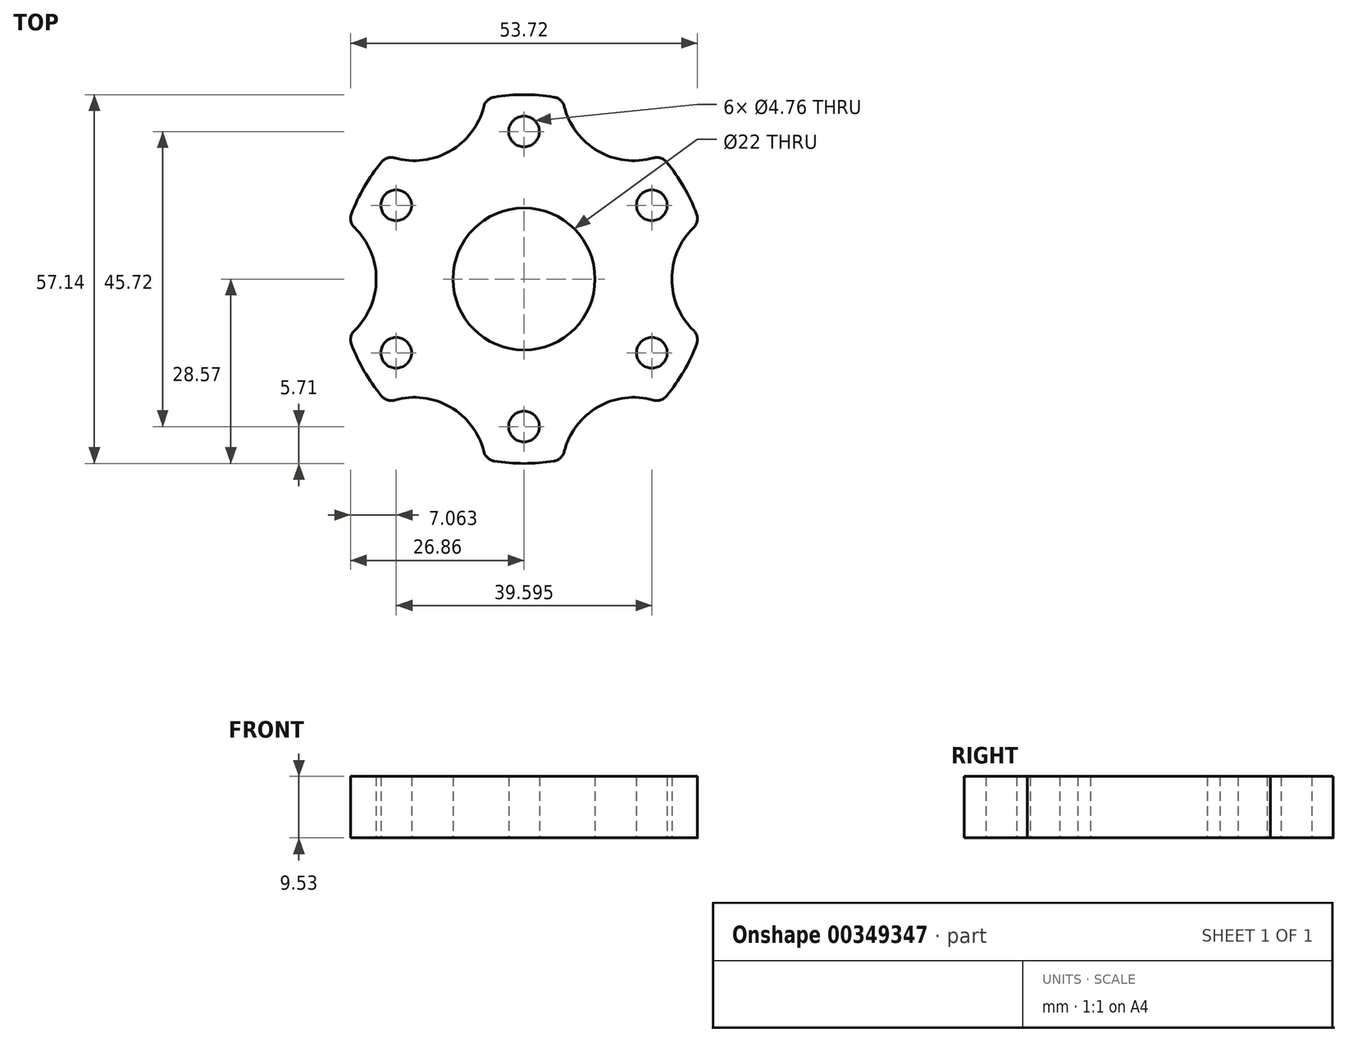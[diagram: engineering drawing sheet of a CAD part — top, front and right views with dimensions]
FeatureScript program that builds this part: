
annotation { "Feature Type Name" : "Feature", "Feature Type Description" : "" }
export const myFeature = defineFeature(function(context is Context, id is Id, definition is map)
    precondition{}
    {
        {
            var Q0;
            Q0=qCreatedBy(makeId("Top.planeOp"),FACE);
            var sketch = newSketch(context, id + "F0", { "sketchPlane" : qUnion([Q0])});
            skCircle(sketch, "E0", {"center": v(0, 0) * mm, "radius": 28.58 * mm});
            skCircle(sketch, "E1", {"center": v(0, 0) * mm, "radius": 11 * mm});
            skSolve(sketch);
        }
        {
            var Q0;
            Q0=makeQuery(id+"F0.imprint","IMPRINT",FACE,{"disambiguationData":[TD([[makeQuery(id+"F0.imprint","IMPRINT",EDGE,{"derivedFrom":sQuery(id+"F0.wireOp",EDGE,"E0")}),1.0]])]});
            extrude(context, id + "F1", {"entities" : qUnion([Q0]), "depth" : 9.52 * mm});
        }
        {
            var Q0;
            Q0=qCreatedBy(makeId("Top.planeOp"),FACE);
            var sketch = newSketch(context, id + "F2", { "sketchPlane" : qUnion([Q0])});
            skCircle(sketch, "E2", {"center": v(0, 0) * mm, "radius": 34.01 * mm});
            skCircle(sketch, "E3", {"center": v(-34.01, 0) * mm, "radius": 11.11 * mm});
            skCircle(sketch, "E4.1.0", {"center": v(-17, -29.45) * mm, "radius": 11.11 * mm});
            skCircle(sketch, "E4.2.0", {"center": v(17, -29.45) * mm, "radius": 11.11 * mm});
            skCircle(sketch, "E4.3.0", {"center": v(34.01, 0) * mm, "radius": 11.11 * mm});
            skCircle(sketch, "E4.4.0", {"center": v(17, 29.45) * mm, "radius": 11.11 * mm});
            skCircle(sketch, "E4.5.0", {"center": v(-17, 29.45) * mm, "radius": 11.11 * mm});
            skSolve(sketch);
        }
        {
            var Q0;
            {var subQ0=sQuery(id+"F2.wireOp",EDGE,"E4.2.0");var subQ1=sQuery(id+"F2.wireOp",EDGE,"E2");var subQ2=makeQuery(id+"F2.imprint","INTERSECT",VERTEX,{"disambiguationData":[OD(0.0)],"derivedFrom":[subQ1,subQ0]});Q0=makeQuery(id+"F2.imprint","IMPRINT",FACE,{"disambiguationData":[TD([[makeQuery(id+"F2.imprint","IMPRINT",EDGE,{"disambiguationData":[TD([[subQ2,-1.0]])],"derivedFrom":subQ1}),1.0]])]});}
            var Q1;
            {var subQ0=sQuery(id+"F2.wireOp",EDGE,"E4.1.0");var subQ1=sQuery(id+"F2.wireOp",EDGE,"E2");var subQ2=makeQuery(id+"F2.imprint","INTERSECT",VERTEX,{"disambiguationData":[OD(0.0)],"derivedFrom":[subQ1,subQ0]});Q1=makeQuery(id+"F2.imprint","IMPRINT",FACE,{"disambiguationData":[TD([[makeQuery(id+"F2.imprint","IMPRINT",EDGE,{"disambiguationData":[TD([[subQ2,-1.0]])],"derivedFrom":subQ1}),1.0]])]});}
            var Q2;
            {var subQ0=sQuery(id+"F2.wireOp",EDGE,"E3");var subQ1=sQuery(id+"F2.wireOp",EDGE,"E2");var subQ2=makeQuery(id+"F2.imprint","INTERSECT",VERTEX,{"disambiguationData":[OD(0.0)],"derivedFrom":[subQ1,subQ0]});Q2=makeQuery(id+"F2.imprint","IMPRINT",FACE,{"disambiguationData":[TD([[makeQuery(id+"F2.imprint","IMPRINT",EDGE,{"disambiguationData":[TD([[subQ2,-1.0]])],"derivedFrom":subQ1}),1.0]])]});}
            var Q3;
            {var subQ0=sQuery(id+"F2.wireOp",EDGE,"E4.5.0");var subQ1=sQuery(id+"F2.wireOp",EDGE,"E2");var subQ2=makeQuery(id+"F2.imprint","INTERSECT",VERTEX,{"disambiguationData":[OD(0.0)],"derivedFrom":[subQ1,subQ0]});Q3=makeQuery(id+"F2.imprint","IMPRINT",FACE,{"disambiguationData":[TD([[makeQuery(id+"F2.imprint","IMPRINT",EDGE,{"disambiguationData":[TD([[subQ2,-1.0]])],"derivedFrom":subQ1}),1.0]])]});}
            var Q4;
            {var subQ0=sQuery(id+"F2.wireOp",EDGE,"E4.4.0");var subQ1=sQuery(id+"F2.wireOp",EDGE,"E2");var subQ2=makeQuery(id+"F2.imprint","INTERSECT",VERTEX,{"disambiguationData":[OD(0.0)],"derivedFrom":[subQ1,subQ0]});Q4=makeQuery(id+"F2.imprint","IMPRINT",FACE,{"disambiguationData":[TD([[makeQuery(id+"F2.imprint","IMPRINT",EDGE,{"disambiguationData":[TD([[subQ2,-1.0]])],"derivedFrom":subQ1}),1.0]])]});}
            var Q5;
            {var subQ0=sQuery(id+"F2.wireOp",EDGE,"E4.3.0");var subQ1=sQuery(id+"F2.wireOp",EDGE,"E2");var subQ2=makeQuery(id+"F2.imprint","INTERSECT",VERTEX,{"disambiguationData":[OD(0.0)],"derivedFrom":[subQ1,subQ0]});Q5=makeQuery(id+"F2.imprint","IMPRINT",FACE,{"disambiguationData":[TD([[makeQuery(id+"F2.imprint","IMPRINT",EDGE,{"disambiguationData":[TD([[subQ2,1.0]])],"derivedFrom":subQ1}),1.0]])]});}
            extrude(context, id + "F3", {"entities" : qUnion([Q0, Q1, Q2, Q3, Q4, Q5]), "operationType" : NewBodyOperationType.REMOVE, "depth" : 25.4 * mm});
        }
        {
            var Q0;
            Q0=qCreatedBy(makeId("Top.planeOp"),FACE);
            var sketch = newSketch(context, id + "F4", { "sketchPlane" : qUnion([Q0])});
            skCircle(sketch, "E5", {"center": v(0, 22.86) * mm, "radius": 2.38 * mm});
            skCircle(sketch, "E6.1.0", {"center": v(-19.8, 11.43) * mm, "radius": 2.38 * mm});
            skCircle(sketch, "E6.2.0", {"center": v(-19.8, -11.43) * mm, "radius": 2.38 * mm});
            skCircle(sketch, "E6.3.0", {"center": v(0, -22.86) * mm, "radius": 2.38 * mm});
            skCircle(sketch, "E6.4.0", {"center": v(19.8, -11.43) * mm, "radius": 2.38 * mm});
            skCircle(sketch, "E6.5.0", {"center": v(19.8, 11.43) * mm, "radius": 2.38 * mm});
            skPoint(sketch, "E6.center", {"position": v(0, 0) * mm});
            skSolve(sketch);
        }
        {
            var Q0;
            Q0 = qSketchRegion(id + "F4", true);
            extrude(context, id + "F5", {"entities" : qUnion([Q0]), "operationType" : NewBodyOperationType.REMOVE, "depth" : 25.4 * mm});
        }
        {
            var Q0;
            Q0=makeQuery(id+"F3.boolean.opBoolean","INTERSECT",EDGE,{"disambiguationData":[OD(0.0)],"derivedFrom":[makeQuery(id+"F1.opExtrude","SWEPT_FACE",FACE,{"disambiguationData":[OSD([sQuery(id+"F0.wireOp",EDGE,"E0")])]}),makeQuery(id+"F3.opExtrude","SWEPT_FACE",FACE,{"disambiguationData":[OSD([sQuery(id+"F2.wireOp",EDGE,"E4.1.0")])]})]});
            var Q1;
            Q1=makeQuery(id+"F3.boolean.opBoolean","INTERSECT",EDGE,{"disambiguationData":[OD(0.0)],"derivedFrom":[makeQuery(id+"F1.opExtrude","SWEPT_FACE",FACE,{"disambiguationData":[OSD([sQuery(id+"F0.wireOp",EDGE,"E0")])]}),makeQuery(id+"F3.opExtrude","SWEPT_FACE",FACE,{"disambiguationData":[OSD([sQuery(id+"F2.wireOp",EDGE,"E3")])]})]});
            var Q2;
            Q2=makeQuery(id+"F3.boolean.opBoolean","INTERSECT",EDGE,{"disambiguationData":[OD(1.0)],"derivedFrom":[makeQuery(id+"F1.opExtrude","SWEPT_FACE",FACE,{"disambiguationData":[OSD([sQuery(id+"F0.wireOp",EDGE,"E0")])]}),makeQuery(id+"F3.opExtrude","SWEPT_FACE",FACE,{"disambiguationData":[OSD([sQuery(id+"F2.wireOp",EDGE,"E3")])]})]});
            var Q3;
            Q3=makeQuery(id+"F3.boolean.opBoolean","INTERSECT",EDGE,{"disambiguationData":[OD(0.0)],"derivedFrom":[makeQuery(id+"F1.opExtrude","SWEPT_FACE",FACE,{"disambiguationData":[OSD([sQuery(id+"F0.wireOp",EDGE,"E0")])]}),makeQuery(id+"F3.opExtrude","SWEPT_FACE",FACE,{"disambiguationData":[OSD([sQuery(id+"F2.wireOp",EDGE,"E4.5.0")])]})]});
            var Q4;
            Q4=makeQuery(id+"F3.boolean.opBoolean","INTERSECT",EDGE,{"disambiguationData":[OD(1.0)],"derivedFrom":[makeQuery(id+"F1.opExtrude","SWEPT_FACE",FACE,{"disambiguationData":[OSD([sQuery(id+"F0.wireOp",EDGE,"E0")])]}),makeQuery(id+"F3.opExtrude","SWEPT_FACE",FACE,{"disambiguationData":[OSD([sQuery(id+"F2.wireOp",EDGE,"E4.5.0")])]})]});
            var Q5;
            Q5=makeQuery(id+"F3.boolean.opBoolean","INTERSECT",EDGE,{"disambiguationData":[OD(1.0)],"derivedFrom":[makeQuery(id+"F1.opExtrude","SWEPT_FACE",FACE,{"disambiguationData":[OSD([sQuery(id+"F0.wireOp",EDGE,"E0")])]}),makeQuery(id+"F3.opExtrude","SWEPT_FACE",FACE,{"disambiguationData":[OSD([sQuery(id+"F2.wireOp",EDGE,"E4.4.0")])]})]});
            var Q6;
            Q6=makeQuery(id+"F3.boolean.opBoolean","INTERSECT",EDGE,{"disambiguationData":[OD(0.0)],"derivedFrom":[makeQuery(id+"F1.opExtrude","SWEPT_FACE",FACE,{"disambiguationData":[OSD([sQuery(id+"F0.wireOp",EDGE,"E0")])]}),makeQuery(id+"F3.opExtrude","SWEPT_FACE",FACE,{"disambiguationData":[OSD([sQuery(id+"F2.wireOp",EDGE,"E4.4.0")])]})]});
            var Q7;
            Q7=makeQuery(id+"F3.boolean.opBoolean","INTERSECT",EDGE,{"disambiguationData":[OD(1.0)],"derivedFrom":[makeQuery(id+"F1.opExtrude","SWEPT_FACE",FACE,{"disambiguationData":[OSD([sQuery(id+"F0.wireOp",EDGE,"E0")])]}),makeQuery(id+"F3.opExtrude","SWEPT_FACE",FACE,{"disambiguationData":[OSD([sQuery(id+"F2.wireOp",EDGE,"E4.3.0")])]})]});
            var Q8;
            Q8=makeQuery(id+"F3.boolean.opBoolean","INTERSECT",EDGE,{"disambiguationData":[OD(0.0)],"derivedFrom":[makeQuery(id+"F1.opExtrude","SWEPT_FACE",FACE,{"disambiguationData":[OSD([sQuery(id+"F0.wireOp",EDGE,"E0")])]}),makeQuery(id+"F3.opExtrude","SWEPT_FACE",FACE,{"disambiguationData":[OSD([sQuery(id+"F2.wireOp",EDGE,"E4.3.0")])]})]});
            var Q9;
            Q9=makeQuery(id+"F3.boolean.opBoolean","INTERSECT",EDGE,{"disambiguationData":[OD(1.0)],"derivedFrom":[makeQuery(id+"F1.opExtrude","SWEPT_FACE",FACE,{"disambiguationData":[OSD([sQuery(id+"F0.wireOp",EDGE,"E0")])]}),makeQuery(id+"F3.opExtrude","SWEPT_FACE",FACE,{"disambiguationData":[OSD([sQuery(id+"F2.wireOp",EDGE,"E4.2.0")])]})]});
            var Q10;
            Q10=makeQuery(id+"F3.boolean.opBoolean","INTERSECT",EDGE,{"disambiguationData":[OD(0.0)],"derivedFrom":[makeQuery(id+"F1.opExtrude","SWEPT_FACE",FACE,{"disambiguationData":[OSD([sQuery(id+"F0.wireOp",EDGE,"E0")])]}),makeQuery(id+"F3.opExtrude","SWEPT_FACE",FACE,{"disambiguationData":[OSD([sQuery(id+"F2.wireOp",EDGE,"E4.2.0")])]})]});
            var Q11;
            Q11=makeQuery(id+"F3.boolean.opBoolean","INTERSECT",EDGE,{"disambiguationData":[OD(1.0)],"derivedFrom":[makeQuery(id+"F1.opExtrude","SWEPT_FACE",FACE,{"disambiguationData":[OSD([sQuery(id+"F0.wireOp",EDGE,"E0")])]}),makeQuery(id+"F3.opExtrude","SWEPT_FACE",FACE,{"disambiguationData":[OSD([sQuery(id+"F2.wireOp",EDGE,"E4.1.0")])]})]});
            fillet(context, id + "F6", {"entities" : qUnion([Q0, Q1, Q2, Q3, Q4, Q5, Q6, Q7, Q8, Q9, Q10, Q11]), "radius" : 2 * mm, "tangentPropagation" : true, "allowEdgeOverflow" : false});
        }
    });
